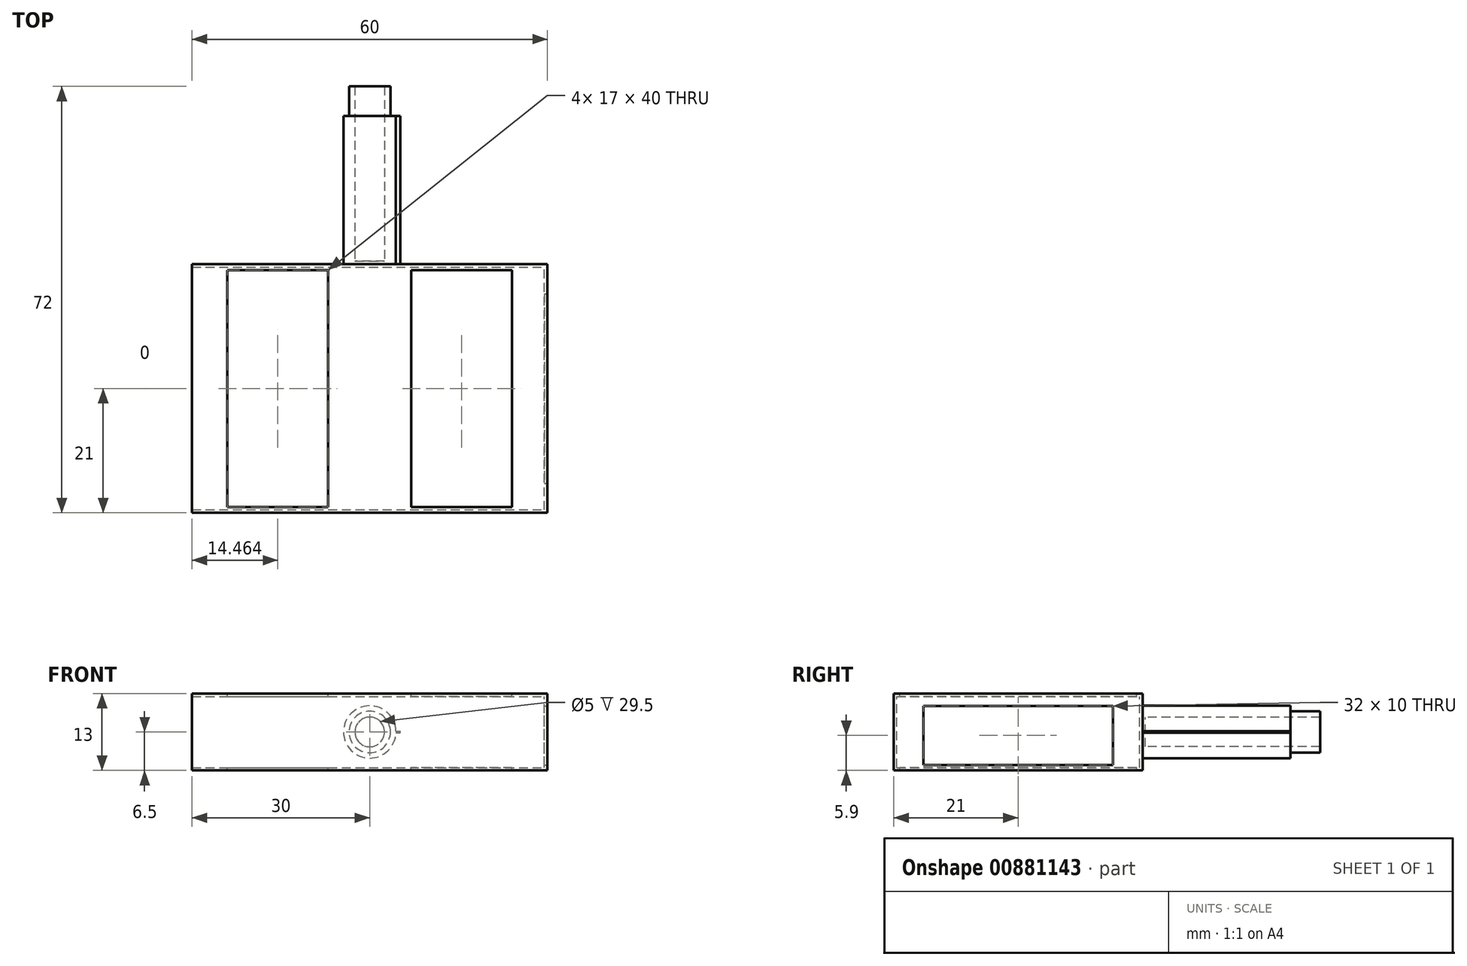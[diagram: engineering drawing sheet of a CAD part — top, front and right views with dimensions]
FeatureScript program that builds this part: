
annotation { "Feature Type Name" : "Feature", "Feature Type Description" : "" }
export const myFeature = defineFeature(function(context is Context, id is Id, definition is map)
    precondition{}
    {
        {
            var Q0;
            Q0=qCreatedBy(makeId("Front.planeOp"),FACE);
            var sketch = newSketch(context, id + "F0", { "sketchPlane" : qUnion([Q0])});
            skLineSegment(sketch, "E0.bottom", {"start": v(0, 0) * mm, "end": v(60, 0) * mm});
            skLineSegment(sketch, "E0.top", {"start": v(0, 13) * mm, "end": v(60, 13) * mm});
            skLineSegment(sketch, "E0.left", {"start": v(0, 0) * mm, "end": v(0, 13) * mm});
            skLineSegment(sketch, "E0.right", {"start": v(60, 0) * mm, "end": v(60, 13) * mm});
            skSolve(sketch);
        }
        {
            var Q0;
            Q0 = qSketchRegion(id + "F0", true);
            extrude(context, id + "F1", {"entities" : qUnion([Q0]), "depth" : 42 * mm, "offsetDistance" : 25 * mm});
        }
        {
            var Q0;
            Q0=makeQuery(id+"F1.opExtrude","SWEPT_FACE",FACE,{"disambiguationData":[OSD([sQuery(id+"F0.wireOp",EDGE,"E0.left")])]});
            shell(context, id + "F2", {"entities" : qUnion([Q0]), "thickness" : 0.5 * mm});
        }
        {
            var Q0;
            Q0=makeQuery(id+"F1.opExtrude","SWEPT_FACE",FACE,{"disambiguationData":[OSD([sQuery(id+"F0.wireOp",EDGE,"E0.right")])]});
            var sketch = newSketch(context, id + "F3", { "sketchPlane" : qUnion([Q0])});
            skLineSegment(sketch, "E1.bottom", {"start": v(-37, 10.9) * mm, "end": v(-5, 10.9) * mm});
            skLineSegment(sketch, "E1.top", {"start": v(-37, 0.9) * mm, "end": v(-5, 0.9) * mm});
            skLineSegment(sketch, "E1.left", {"start": v(-37, 10.9) * mm, "end": v(-37, 0.9) * mm});
            skLineSegment(sketch, "E1.right", {"start": v(-5, 10.9) * mm, "end": v(-5, 0.9) * mm});
            skSolve(sketch);
        }
        {
            var Q0;
            Q0 = qSketchRegion(id + "F3", true);
            extrude(context, id + "F4", {"entities" : qUnion([Q0]), "operationType" : NewBodyOperationType.REMOVE, "oppositeDirection" : true, "depth" : 25 * mm, "offsetDistance" : 25 * mm});
        }
        {
            var Q0;
            Q0=makeQuery(id+"F1.opExtrude","SWEPT_FACE",FACE,{"disambiguationData":[OSD([sQuery(id+"F0.wireOp",EDGE,"E0.top")])]});
            var sketch = newSketch(context, id + "F5", { "sketchPlane" : qUnion([Q0])});
            skLineSegment(sketch, "E2.bottom", {"start": v(5.96, -1) * mm, "end": v(22.96, -1) * mm});
            skLineSegment(sketch, "E2.top", {"start": v(5.96, -41) * mm, "end": v(22.96, -41) * mm});
            skLineSegment(sketch, "E2.left", {"start": v(5.96, -1) * mm, "end": v(5.96, -41) * mm});
            skLineSegment(sketch, "E2.right", {"start": v(22.96, -1) * mm, "end": v(22.96, -41) * mm});
            skLineSegment(sketch, "E3", {"start": v(30, 0) * mm, "end": v(30, -42) * mm, "construction": true});
            skLineSegment(sketch, "E4.MirrorCS", {"start": v(37.04, -1) * mm, "end": v(37.04, -41) * mm});
            skLineSegment(sketch, "E5.MirrorCS", {"start": v(54.04, -41) * mm, "end": v(37.04, -41) * mm});
            skLineSegment(sketch, "E6.MirrorCS", {"start": v(54.04, -1) * mm, "end": v(54.04, -41) * mm});
            skLineSegment(sketch, "E7.MirrorCS", {"start": v(54.04, -1) * mm, "end": v(37.04, -1) * mm});
            skSolve(sketch);
        }
        {
            var Q0;
            Q0 = qSketchRegion(id + "F5", true);
            extrude(context, id + "F6", {"entities" : qUnion([Q0]), "operationType" : NewBodyOperationType.REMOVE, "oppositeDirection" : true, "depth" : 25 * mm, "offsetDistance" : 25 * mm});
        }
        {
            var Q0;
            Q0=makeQuery(id+"F1.opExtrude","CAP_FACE",FACE,{"disambiguationData":[OSD([sQuery(id+"F0.wireOp",EDGE,"E0.bottom"),sQuery(id+"F0.wireOp",EDGE,"E0.top"),sQuery(id+"F0.wireOp",EDGE,"E0.left"),sQuery(id+"F0.wireOp",EDGE,"E0.right")])],"isStart":true});
            var sketch = newSketch(context, id + "F7", { "sketchPlane" : qUnion([Q0])});
            skCircle(sketch, "E8", {"center": v(-30, 6.5) * mm, "radius": 3.5 * mm});
            skPoint(sketch, "E8.centerSnap0", {"position": v(0, 6.5) * mm});
            skPoint(sketch, "E8.centerSnap1", {"position": v(-30, 0) * mm});
            skLineSegment(sketch, "E9", {"start": v(-30, 6.5) * mm, "end": v(-60, 6.5) * mm, "construction": true});
            skSolve(sketch);
        }
        {
            var Q0;
            Q0 = qSketchRegion(id + "F7", true);
            extrude(context, id + "F8", {"entities" : qUnion([Q0]), "operationType" : NewBodyOperationType.ADD, "depth" : 30 * mm, "offsetDistance" : 25 * mm});
        }
        {
            var Q0;
            Q0=makeQuery(id+"F8.opExtrude","CAP_FACE",FACE,{"disambiguationData":[OSD([sQuery(id+"F7.wireOp",EDGE,"E8")])],"isStart":false});
            shell(context, id + "F9", {"entities" : qUnion([Q0]), "thickness" : 1 * mm});
        }
        {
            var Q0;
            Q0=makeQuery(id+"F1.opExtrude","CAP_FACE",FACE,{"disambiguationData":[OSD([sQuery(id+"F0.wireOp",EDGE,"E0.bottom"),sQuery(id+"F0.wireOp",EDGE,"E0.top"),sQuery(id+"F0.wireOp",EDGE,"E0.left"),sQuery(id+"F0.wireOp",EDGE,"E0.right")])],"isStart":true});
            var sketch = newSketch(context, id + "F10", { "sketchPlane" : qUnion([Q0])});
            skCircle(sketch, "E10", {"center": v(-30, 6.5) * mm, "radius": 4.42 * mm});
            skLineSegment(sketch, "E11", {"start": v(-30, 6.5) * mm, "end": v(-53.15, 6.5) * mm, "construction": true});
            skLineSegment(sketch, "E12.bottom", {"start": v(-34.42, 6.39) * mm, "end": v(-35.15, 6.39) * mm});
            skLineSegment(sketch, "E12.top", {"start": v(-34.42, 6.61) * mm, "end": v(-35.15, 6.61) * mm});
            skLineSegment(sketch, "E12.left", {"start": v(-34.42, 6.39) * mm, "end": v(-34.42, 6.61) * mm});
            skLineSegment(sketch, "E12.right", {"start": v(-35.15, 6.39) * mm, "end": v(-35.15, 6.61) * mm});
            skPoint(sketch, "E12.middle", {"position": v(-34.78, 6.5) * mm});
            skSolve(sketch);
        }
        {
            var Q0;
            Q0=makeQuery(id+"F10.imprint","IMPRINT",FACE,{"disambiguationData":[TD([[makeQuery(id+"F10.imprint","IMPRINT",EDGE,{"derivedFrom":sQuery(id+"F10.wireOp",EDGE,"E10")}),1.0]])]});
            var Q1;
            {var subQ1=sQuery(id+"F10.wireOp",EDGE,"E12.bottom");Q1=makeQuery(id+"F10.imprint","IMPRINT",FACE,{"disambiguationData":[TD([[makeQuery(id+"F10.imprint","IMPRINT",EDGE,{"derivedFrom":subQ1}),-1.0]])]});}
            var Q2;
            {var subQ0=sQuery(id+"F10.wireOp",EDGE,"E12.left");Q2=makeQuery(id+"F10.imprint","IMPRINT",FACE,{"disambiguationData":[TD([[makeQuery(id+"F10.imprint","IMPRINT",EDGE,{"derivedFrom":subQ0}),-1.0]])]});}
            extrude(context, id + "F11", {"entities" : qUnion([Q0, Q1, Q2]), "operationType" : NewBodyOperationType.ADD, "depth" : 25 * mm, "offsetDistance" : 25 * mm});
        }
    });
